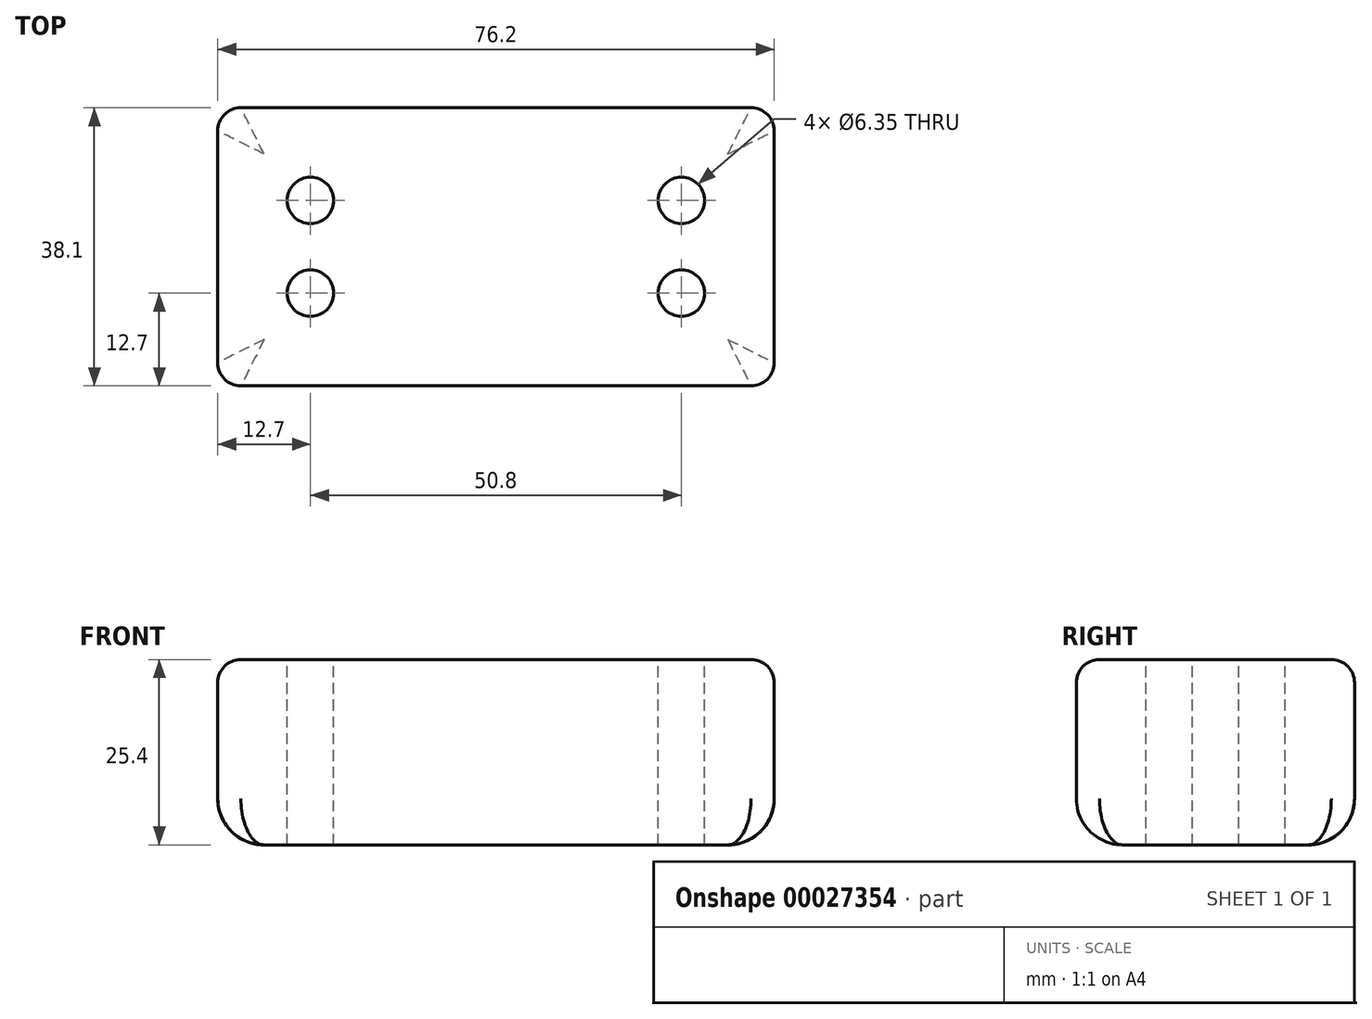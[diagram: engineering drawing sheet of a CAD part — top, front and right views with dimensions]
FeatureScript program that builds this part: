
annotation { "Feature Type Name" : "Feature", "Feature Type Description" : "" }
export const myFeature = defineFeature(function(context is Context, id is Id, definition is map)
    precondition{}
    {
        {
            var Q0;
            Q0=qCreatedBy(makeId("Top.planeOp"),FACE);
            var sketch = newSketch(context, id + "F0", { "sketchPlane" : qUnion([Q0])});
            skLineSegment(sketch, "E0.bottom", {"start": v(0, 0) * mm, "end": v(76.2, 0) * mm});
            skLineSegment(sketch, "E0.top", {"start": v(0, -38.1) * mm, "end": v(76.2, -38.1) * mm});
            skLineSegment(sketch, "E0.left", {"start": v(0, 0) * mm, "end": v(0, -38.1) * mm});
            skLineSegment(sketch, "E0.right", {"start": v(76.2, 0) * mm, "end": v(76.2, -38.1) * mm});
            skSolve(sketch);
        }
        {
            var Q0;
            Q0=makeQuery(id+"F0.imprint","IMPRINT",FACE,{"disambiguationData":[TD([[makeQuery(id+"F0.imprint","IMPRINT",EDGE,{"derivedFrom":sQuery(id+"F0.wireOp",EDGE,"E0.bottom")}),-1.0]])]});
            extrude(context, id + "F1", {"entities" : qUnion([Q0]), "depth" : 25.4 * mm});
        }
        {
            var Q0;
            Q0=makeQuery(id+"F1.opExtrude","SWEPT_EDGE",EDGE,{"disambiguationData":[OSD([sQuery(id+"F0.wireOp",EDGE,"E0.top"),sQuery(id+"F0.wireOp",EDGE,"E0.left")])]});
            var Q1;
            Q1=makeQuery(id+"F1.opExtrude","SWEPT_EDGE",EDGE,{"disambiguationData":[OSD([sQuery(id+"F0.wireOp",EDGE,"E0.bottom"),sQuery(id+"F0.wireOp",EDGE,"E0.left")])]});
            var Q2;
            Q2=makeQuery(id+"F1.opExtrude","SWEPT_EDGE",EDGE,{"disambiguationData":[OSD([sQuery(id+"F0.wireOp",EDGE,"E0.bottom"),sQuery(id+"F0.wireOp",EDGE,"E0.right")])]});
            var Q3;
            Q3=makeQuery(id+"F1.opExtrude","SWEPT_EDGE",EDGE,{"disambiguationData":[OSD([sQuery(id+"F0.wireOp",EDGE,"E0.top"),sQuery(id+"F0.wireOp",EDGE,"E0.right")])]});
            var Q4;
            Q4=makeQuery(id+"F1.opExtrude","CAP_FACE",FACE,{"disambiguationData":[OSD([sQuery(id+"F0.wireOp",EDGE,"E0.bottom"),sQuery(id+"F0.wireOp",EDGE,"E0.top"),sQuery(id+"F0.wireOp",EDGE,"E0.left"),sQuery(id+"F0.wireOp",EDGE,"E0.right")])],"isStart":false});
            fillet(context, id + "F2", {"entities" : qUnion([Q0, Q1, Q2, Q3, Q4]), "radius" : 3.17 * mm, "tangentPropagation" : true, "allowEdgeOverflow" : false});
        }
        {
            var Q0;
            Q0=makeQuery(id+"F1.opExtrude","CAP_FACE",FACE,{"disambiguationData":[OSD([sQuery(id+"F0.wireOp",EDGE,"E0.bottom"),sQuery(id+"F0.wireOp",EDGE,"E0.top"),sQuery(id+"F0.wireOp",EDGE,"E0.left"),sQuery(id+"F0.wireOp",EDGE,"E0.right")])],"isStart":true});
            fillet(context, id + "F3", {"entities" : qUnion([Q0]), "radius" : 6.35 * mm, "tangentPropagation" : true, "allowEdgeOverflow" : false});
        }
        {
            var Q0;
            Q0=makeQuery(id+"F1.opExtrude","CAP_FACE",FACE,{"disambiguationData":[OSD([sQuery(id+"F0.wireOp",EDGE,"E0.bottom"),sQuery(id+"F0.wireOp",EDGE,"E0.top"),sQuery(id+"F0.wireOp",EDGE,"E0.left"),sQuery(id+"F0.wireOp",EDGE,"E0.right")])],"isStart":false});
            var sketch = newSketch(context, id + "F4", { "sketchPlane" : qUnion([Q0])});
            skPoint(sketch, "E1", {"position": v(12.7, -25.4) * mm});
            skPoint(sketch, "E2", {"position": v(12.7, -12.7) * mm});
            skPoint(sketch, "E3", {"position": v(63.5, -12.7) * mm});
            skPoint(sketch, "E4", {"position": v(63.5, -25.4) * mm});
            skSolve(sketch);
        }
        {
            var Q0;
            Q0=sQuery(id+"F4.wireOp",VERTEX,"E2");
            var Q1;
            Q1=sQuery(id+"F4.wireOp",VERTEX,"E1");
            var Q2;
            Q2=sQuery(id+"F4.wireOp",VERTEX,"E4");
            var Q3;
            Q3=sQuery(id+"F4.wireOp",VERTEX,"E3");
            var Q4;
            Q4=makeQuery(id+"F1.opExtrude","SWEPT_BODY",BODY,{"disambiguationData":[OSD([sQuery(id+"F0.wireOp",EDGE,"E0.bottom"),sQuery(id+"F0.wireOp",EDGE,"E0.top"),sQuery(id+"F0.wireOp",EDGE,"E0.left"),sQuery(id+"F0.wireOp",EDGE,"E0.right")])]});
            hole(context, id + "F5", {"style" : HoleStyle.SIMPLE, "holeDiameter" : 6.35 * mm, "endStyle" : HoleEndStyle.THROUGH, "locations" : qUnion([Q0, Q1, Q2, Q3]), "scope" : qUnion([Q4])});
        }
    });
